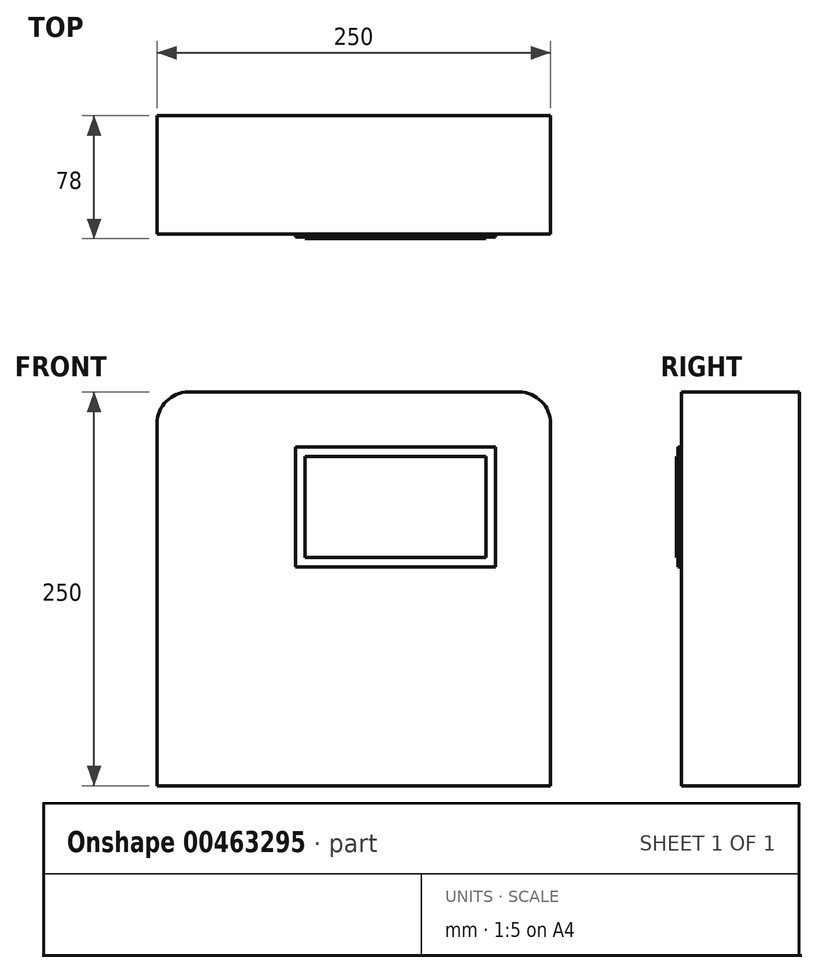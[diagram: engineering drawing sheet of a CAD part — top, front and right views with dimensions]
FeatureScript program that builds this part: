
annotation { "Feature Type Name" : "Feature", "Feature Type Description" : "" }
export const myFeature = defineFeature(function(context is Context, id is Id, definition is map)
    precondition{}
    {
        {
            var Q0;
            Q0=qCreatedBy(makeId("Front.planeOp"),FACE);
            var sketch = newSketch(context, id + "F0", { "sketchPlane" : qUnion([Q0])});
            skLineSegment(sketch, "E0.bottom", {"start": v(125, 125) * mm, "end": v(-125, 125) * mm});
            skLineSegment(sketch, "E0.top", {"start": v(125, -125) * mm, "end": v(-125, -125) * mm});
            skLineSegment(sketch, "E0.left", {"start": v(125, 125) * mm, "end": v(125, -125) * mm});
            skLineSegment(sketch, "E0.right", {"start": v(-125, 125) * mm, "end": v(-125, -125) * mm});
            skPoint(sketch, "E0.middle", {"position": v(0, 0) * mm});
            skSolve(sketch);
        }
        {
            var Q0;
            Q0=makeQuery(id+"F0.imprint","IMPRINT",FACE,{"disambiguationData":[TD([[makeQuery(id+"F0.imprint","IMPRINT",EDGE,{"derivedFrom":sQuery(id+"F0.wireOp",EDGE,"E0.bottom")}),1.0]])]});
            extrude(context, id + "F1", {"entities" : qUnion([Q0]), "endBound" : BoundingType.SYMMETRIC, "depth" : 75 * mm});
        }
        {
            var Q0;
            Q0=makeQuery(id+"F1.opExtrude","SWEPT_EDGE",EDGE,{"disambiguationData":[OSD([sQuery(id+"F0.wireOp",EDGE,"E0.bottom"),sQuery(id+"F0.wireOp",EDGE,"E0.left")])]});
            var Q1;
            Q1=makeQuery(id+"F1.opExtrude","SWEPT_EDGE",EDGE,{"disambiguationData":[OSD([sQuery(id+"F0.wireOp",EDGE,"E0.bottom"),sQuery(id+"F0.wireOp",EDGE,"E0.right")])]});
            fillet(context, id + "F2", {"entities" : qUnion([Q0, Q1]), "radius" : 20 * mm, "tangentPropagation" : true, "allowEdgeOverflow" : false});
        }
        {
            var Q0;
            Q0=makeQuery(id+"F1.opExtrude","CAP_FACE",FACE,{"disambiguationData":[OSD([sQuery(id+"F0.wireOp",EDGE,"E0.bottom"),sQuery(id+"F0.wireOp",EDGE,"E0.top"),sQuery(id+"F0.wireOp",EDGE,"E0.left"),sQuery(id+"F0.wireOp",EDGE,"E0.right")])],"isStart":false});
            var sketch = newSketch(context, id + "F3", { "sketchPlane" : qUnion([Q0])});
            skLineSegment(sketch, "E1.bottom", {"start": v(90, 90) * mm, "end": v(-37, 90) * mm});
            skLineSegment(sketch, "E1.top", {"start": v(90, 14) * mm, "end": v(-37, 14) * mm});
            skLineSegment(sketch, "E1.left", {"start": v(90, 90) * mm, "end": v(90, 14) * mm});
            skLineSegment(sketch, "E1.right", {"start": v(-37, 90) * mm, "end": v(-37, 14) * mm});
            skPoint(sketch, "E1.middle", {"position": v(26.5, 52) * mm});
            skSolve(sketch);
        }
        {
            var Q0;
            Q0=makeQuery(id+"F3.imprint","IMPRINT",FACE,{"disambiguationData":[TD([[makeQuery(id+"F3.imprint","IMPRINT",EDGE,{"derivedFrom":sQuery(id+"F3.wireOp",EDGE,"E1.bottom")}),1.0]])]});
            extrude(context, id + "F4", {"entities" : qUnion([Q0]), "depth" : 2 * mm});
        }
        {
            var Q0;
            Q0=makeQuery(id+"F4.opExtrude","CAP_FACE",FACE,{"disambiguationData":[OSD([sQuery(id+"F3.wireOp",EDGE,"E1.bottom"),sQuery(id+"F3.wireOp",EDGE,"E1.top"),sQuery(id+"F3.wireOp",EDGE,"E1.left"),sQuery(id+"F3.wireOp",EDGE,"E1.right")])],"isStart":false});
            var sketch = newSketch(context, id + "F5", { "sketchPlane" : qUnion([Q0])});
            skLineSegment(sketch, "E2.bottom", {"start": v(84, 84) * mm, "end": v(-31, 84) * mm});
            skLineSegment(sketch, "E2.top", {"start": v(84, 20) * mm, "end": v(-31, 20) * mm});
            skLineSegment(sketch, "E2.left", {"start": v(84, 84) * mm, "end": v(84, 20) * mm});
            skLineSegment(sketch, "E2.right", {"start": v(-31, 84) * mm, "end": v(-31, 20) * mm});
            skPoint(sketch, "E2.middle", {"position": v(26.5, 52) * mm});
            skSolve(sketch);
        }
        {
            var Q0;
            Q0=makeQuery(id+"F5.imprint","IMPRINT",FACE,{"disambiguationData":[TD([[makeQuery(id+"F5.imprint","IMPRINT",EDGE,{"derivedFrom":sQuery(id+"F5.wireOp",EDGE,"E2.bottom")}),1.0]])]});
            extrude(context, id + "F6", {"entities" : qUnion([Q0]), "operationType" : NewBodyOperationType.ADD, "depth" : 1 * mm});
        }
    });
